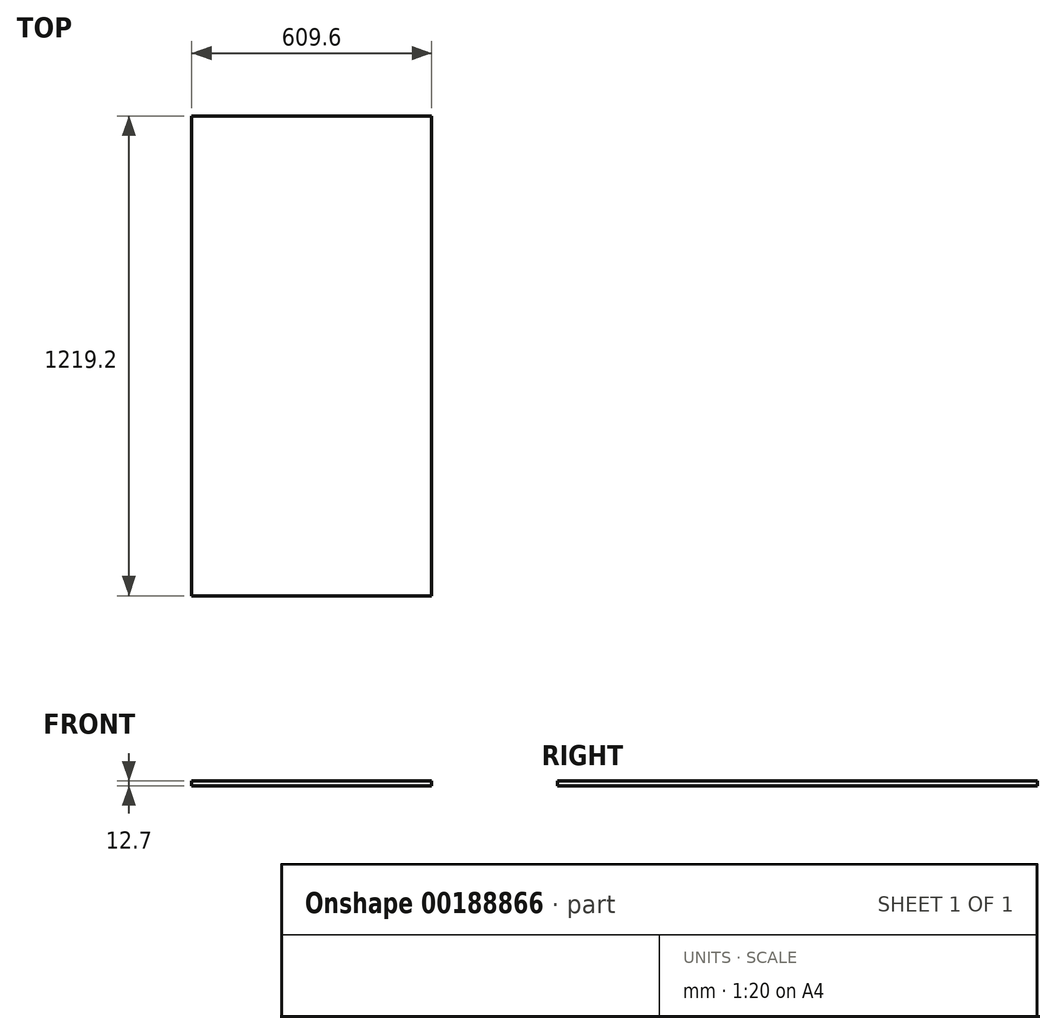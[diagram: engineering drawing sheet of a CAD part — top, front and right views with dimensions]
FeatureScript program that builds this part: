
annotation { "Feature Type Name" : "Feature", "Feature Type Description" : "" }
export const myFeature = defineFeature(function(context is Context, id is Id, definition is map)
    precondition{}
    {
        {
            var Q0;
            Q0=qCreatedBy(makeId("Top.planeOp"), FACE);
            var sketch = newSketch(context, id + "F0", { "sketchPlane" : qUnion([Q0])});
            skLineSegment(sketch, "E0.bottom", {"start": v(304.8, -609.6) * mm, "end": v(-304.8, -609.6) * mm});
            skLineSegment(sketch, "E0.top", {"start": v(304.8, 609.6) * mm, "end": v(-304.8, 609.6) * mm});
            skLineSegment(sketch, "E0.left", {"start": v(304.8, -609.6) * mm, "end": v(304.8, 609.6) * mm});
            skLineSegment(sketch, "E0.right", {"start": v(-304.8, -609.6) * mm, "end": v(-304.8, 609.6) * mm});
            skPoint(sketch, "E0.middle", {"position": v(0, 0) * mm});
            skSolve(sketch);
        }
        {
            var Q0;
            Q0 = qSketchRegion(id + "F0", true);
            extrude(context, id + "F1", {"entities" : qUnion([Q0]), "depth" : 12.7 * mm, "offsetDistance" : 25.4 * mm});
        }
    });
